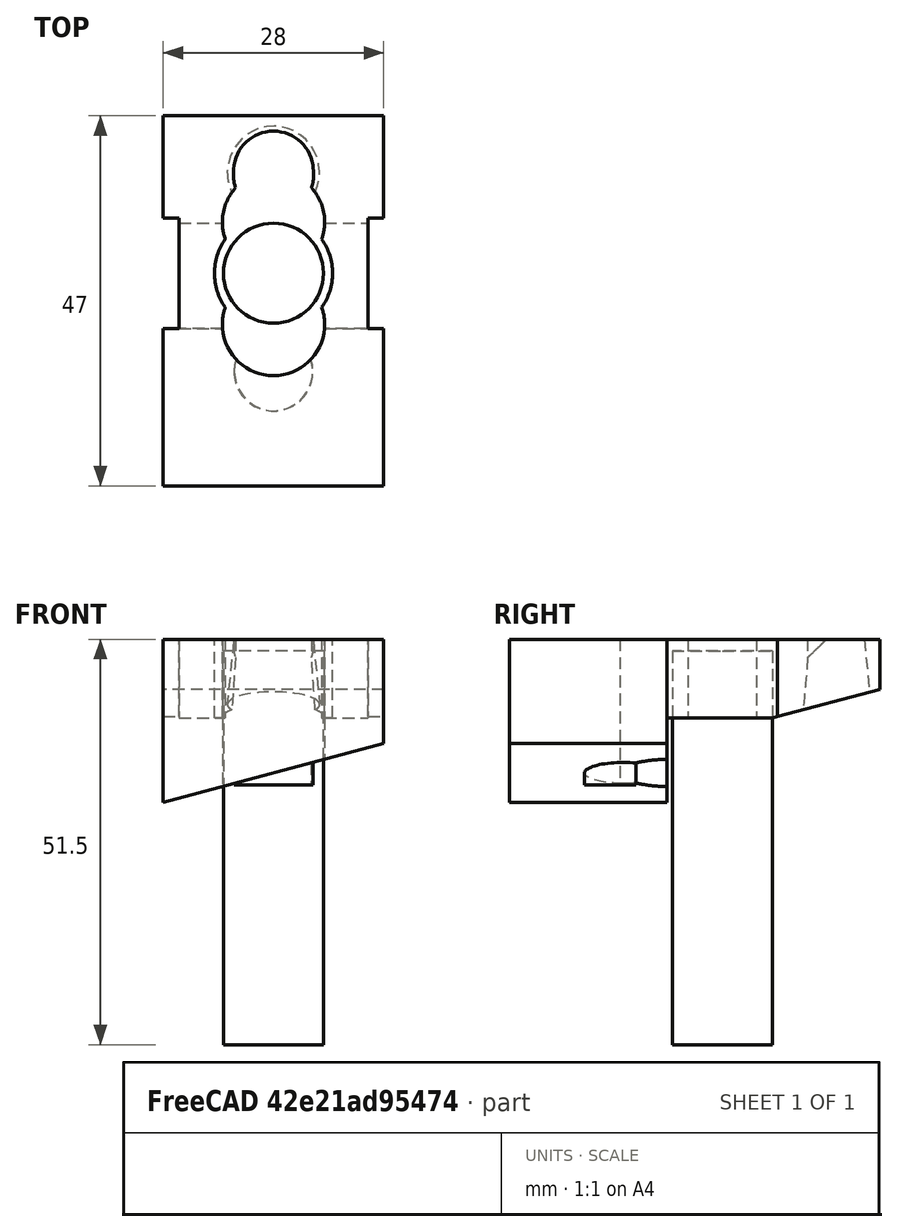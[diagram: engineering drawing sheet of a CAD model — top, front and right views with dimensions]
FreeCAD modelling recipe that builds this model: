
FCSTD DOCUMENT  (FreeCAD 0.20R29410 (Git))
Label: laddleFour4
License: All rights reserved
LicenseURL: http://en.wikipedia.org/wiki/All_rights_reserved
objects: Part::Cylinder×11, Part::MultiFuse×10, Part::Box×8, Part::Cut×8, Part::Cone×1, Part::Feature×1
note: 39 computed .brp shape members not serialized (recipe doc carries the construction recipe); baked Part::Feature solids carry a one-line shape summary decoded from their .brp

FEATURE [Part::Box] Box  label="Cube"
  AttacherType = Attacher::AttachEngine3D
  Height = 30
  Length = 40
  Placement = pos=(-19.5582,7,39.7598) rot=(0,1,0;0.261799rad)
  Width = 20
FEATURE [Part::Box] Box001  label="Cube001"
  AttacherType = Attacher::AttachEngine3D
  Height = 30
  Length = 40
  Placement = pos=(-19.5582,7,39.7598) rot=(0,1,0;0.261799rad)
  Width = 20
FEATURE [Part::Cylinder] Cylinder001
  Angle = 360
  AttacherType = Attacher::AttachEngine3D
  FirstAngle = 0
  Height = 50
  Placement = pos=(0,12.5,0) rot=(0,0,1;0rad)
  Radius = 5
  SecondAngle = 0
FEATURE [Part::Cylinder] Cylinder003  label="bevilPin"
  Angle = 360
  AttacherType = Attacher::AttachEngine3D
  FirstAngle = 0
  Height = 50
  Radius = 6.35
  SecondAngle = 0
FEATURE [Part::Cylinder] Cylinder004  label="bevilPin001"
  Angle = 360
  AttacherType = Attacher::AttachEngine3D
  FirstAngle = 0
  Height = 50
  Radius = 6.35
  SecondAngle = 0
FEATURE [Part::Cylinder] Cylinder005
  Angle = 360
  AttacherType = Attacher::AttachEngine3D
  FirstAngle = 0
  Height = 50
  Placement = pos=(0,12.5,0) rot=(0,0,1;0rad)
  Radius = 5
  SecondAngle = 0
FEATURE [Part::Cylinder] Cylinder006  label="bevilPin002"
  Angle = 360
  AttacherType = Attacher::AttachEngine3D
  FirstAngle = 0
  Height = 50
  Radius = 6.35
  SecondAngle = 0
FEATURE [Part::MultiFuse] Fusion
  Shapes = -> [Cylinder001,Box]
FEATURE [Part::MultiFuse] Fusion001
  Shapes = -> [Fusion,Cylinder004]
FEATURE [Part::MultiFuse] Fusion002
  Shapes = -> [Cylinder005,Box001]
FEATURE [Part::MultiFuse] Fusion003
  Placement = pos=(0,0,0) rot=(0,0,1;3.14159rad)
  Shapes = -> [Fusion002,Cylinder006]
FEATURE [Part::MultiFuse] Fusion004
  Shapes = -> [Fusion003,Fusion001]
FEATURE [Part::Box] Box002  label="Cube002"
  AttacherType = Attacher::AttachEngine3D
  Height = 10
  Length = 24
  Placement = pos=(-12,-13,41.5) rot=(0,0,1;0rad)
  Width = 39
FEATURE [Part::Box] Box003  label="Cube003"
  AttacherType = Attacher::AttachEngine3D
  Height = 20
  Length = 57
  Placement = pos=(-29.5,-29,51.5) rot=(0,0,1;0rad)
  Width = 59
FEATURE [Part::MultiFuse] Fusion005
  Shapes = -> [Box002,Fusion004]
FEATURE [Part::Cut] Cut
  Base = -> Fusion005
  Tool = -> Box003
FEATURE [Part::Cylinder] Cylinder007  label="bevilPin003"
  Angle = 360
  AttacherType = Attacher::AttachEngine3D
  FirstAngle = 0
  Height = 70
  Radius = 7.5
  SecondAngle = 0
FEATURE [Part::Cylinder] Cylinder008
  Angle = 360
  AttacherType = Attacher::AttachEngine3D
  FirstAngle = 0
  Height = 70
  Placement = pos=(0,12.5,0) rot=(0,0,1;0rad)
  Radius = 5.1
  SecondAngle = 0
FEATURE [Part::Cylinder] Cylinder009
  Angle = 360
  AttacherType = Attacher::AttachEngine3D
  FirstAngle = 0
  Height = 70
  Placement = pos=(0,6.5,0) rot=(0,0,1;0rad)
  Radius = 6.5
  SecondAngle = 0
FEATURE [Part::MultiFuse] Fusion006
  Shapes = -> [Cylinder009,Cylinder007]
FEATURE [Part::Cylinder] Cylinder010  label="bevilPin004"
  Angle = 360
  AttacherType = Attacher::AttachEngine3D
  FirstAngle = 0
  Height = 70
  Radius = 7.5
  SecondAngle = 0
FEATURE [Part::Cylinder] Cylinder011
  Angle = 360
  AttacherType = Attacher::AttachEngine3D
  FirstAngle = 0
  Height = 70
  Placement = pos=(0,6.5,0) rot=(0,0,1;0rad)
  Radius = 6.5
  SecondAngle = 0
FEATURE [Part::MultiFuse] Fusion007
  Placement = pos=(0,0,0) rot=(0,0,1;3.14159rad)
  Shapes = -> [Cylinder011,Cylinder010]
FEATURE [Part::MultiFuse] Fusion008
  Shapes = -> [Fusion007,Fusion006]
FEATURE [Part::Cut] Cut001
  Base = -> Cut
  Tool = -> Cylinder008
FEATURE [Part::Cut] Cut002
  Base = -> Cut001
  Tool = -> Fusion008
FEATURE [Part::Cylinder] Cylinder012  label="bevilPin005"
  Angle = 360
  AttacherType = Attacher::AttachEngine3D
  FirstAngle = 0
  Height = 50
  Placement = pos=(0,-12.5,-17) rot=(0,0,1;0rad)
  Radius = 5.1
  SecondAngle = 0
FEATURE [Part::Cut] Cut003
  Base = -> Cut002
  Tool = -> Cylinder012
FEATURE [Part::Box] Box004  label="Cube004"
  AttacherType = Attacher::AttachEngine3D
  Height = 19
  Length = 50
  Placement = pos=(-24,7.96593,22.2588) rot=(1,0,0;0.261799rad)
  Width = 30
FEATURE [Part::Cut] Cut004
  Base = -> Cut003
  Tool = -> Box004
FEATURE [Part::Box] Box005  label="Cube005"
  AttacherType = Attacher::AttachEngine3D
  Height = 30
  Length = 12
  Placement = pos=(14,-29,23) rot=(0,0,1;0rad)
  Width = 60
FEATURE [Part::Box] Box006  label="Cube006"
  AttacherType = Attacher::AttachEngine3D
  Height = 30
  Length = 12
  Placement = pos=(-26,-29,23) rot=(0,0,1;0rad)
  Width = 60
FEATURE [Part::MultiFuse] Fusion009
  Shapes = -> [Box006,Box005]
FEATURE [Part::Cut] Cut005
  Base = -> Cut004
  Tool = -> Fusion009
FEATURE [Part::Cone] Cone
  Angle = 360
  AttacherType = Attacher::AttachEngine3D
  Height = 10
  Placement = pos=(-1.5e-15,13,52) rot=(0,1,0;3.14159rad)
  Radius1 = 5
  Radius2 = 6
FEATURE [Part::Cut] Cut006
  Base = -> Cut005
  Tool = -> Cone
FEATURE [Part::Box] Box007  label="Cube007"
  AttacherType = Attacher::AttachEngine3D
  Height = 10
  Length = 30
  Placement = pos=(-16,20,42) rot=(0,0,1;0rad)
  Width = 20
FEATURE [Part::Cut] Cut007
  Base = -> Cut006
  Tool = -> Box007
FEATURE [Part::Feature] Cut007_solid  label="Cut007 (Solid)"
  shape: bbox 28 x 47 x 20.73 mm, 37 faces (baked)
